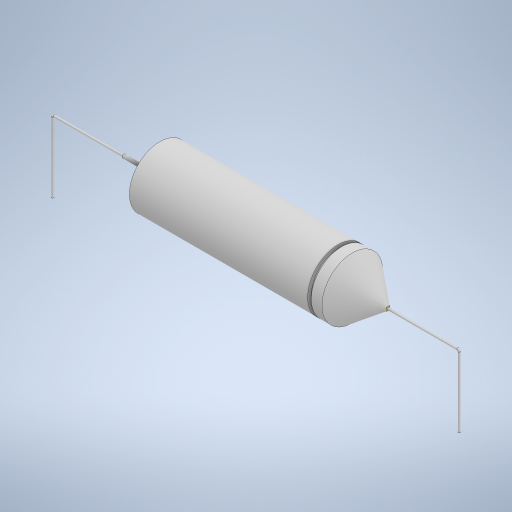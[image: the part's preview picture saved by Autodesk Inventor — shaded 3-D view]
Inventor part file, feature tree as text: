
AUTODESK INVENTOR PART (.ipt)
format: ipt  version: 2024 (Build 280153000, 153)  size: 281,600 bytes
history: native  units: in
note: dims shown in document units (in); Inventor stores cm internally (conversion verified against a paired STEP export)
features: sketch x3, revolve x1, plane x1, sweep x1, mirror x1
ambient origin geometry x8: Origin, YZ Plane, XZ Plane, XY Plane, X Axis, Y Axis, Z Axis, Center Point
bodies: Solid1 (feature_tree)
feature tree (7):
  revolve  "Revolution1"  [1 undecoded]
  sketch  "Sketch2"  dims[d2=0.1575in d8=0.9843in]
  plane  "Work Plane1"
  sweep  "Sweep1"
  mirror  "Mirror1"
  sketch  "Sketch1"  dims[d0=0.0098in d1=0.1969in]
  sketch  "Sketch3"  dims[d9=0.0197in d10=0.0197in d11=0.0197in d12=0.0591in d14=0.0098in d15=90.0deg d16=0.3937in d17=0.3937in d18=0.0079in d19=0.0in d20=0.0118in d21=0.0in d22=0.0in]
note: 1 required parameter value undecoded (feature->parameter linkage not recoverable at this tier; creation-order binding heuristic only, values carry confidence <= 0.55)
